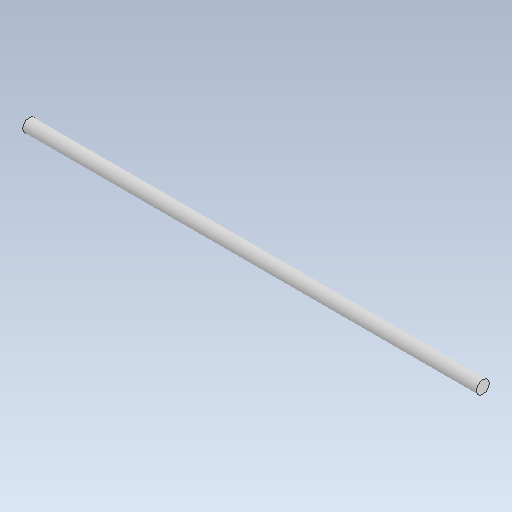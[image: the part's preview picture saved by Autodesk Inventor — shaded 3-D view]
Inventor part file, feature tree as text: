
AUTODESK INVENTOR PART (.ipt)
format: ipt  version: 2021 (Build 250183000, 183)  size: 94,208 bytes
history: native  units: mm
features: extrude x1, sketch x1
ambient origin geometry x8: Origin, YZ Plane, XZ Plane, XY Plane, X Axis, Y Axis, Z Axis, Center Point
bodies: Solid1 (feature_tree)
feature tree (2):
  extrude  "Extrusion1"  Depth=635.0mm
  sketch  "Sketch1"  dims[d0=18.0mm d1=635.0mm d2=0.0mm]
